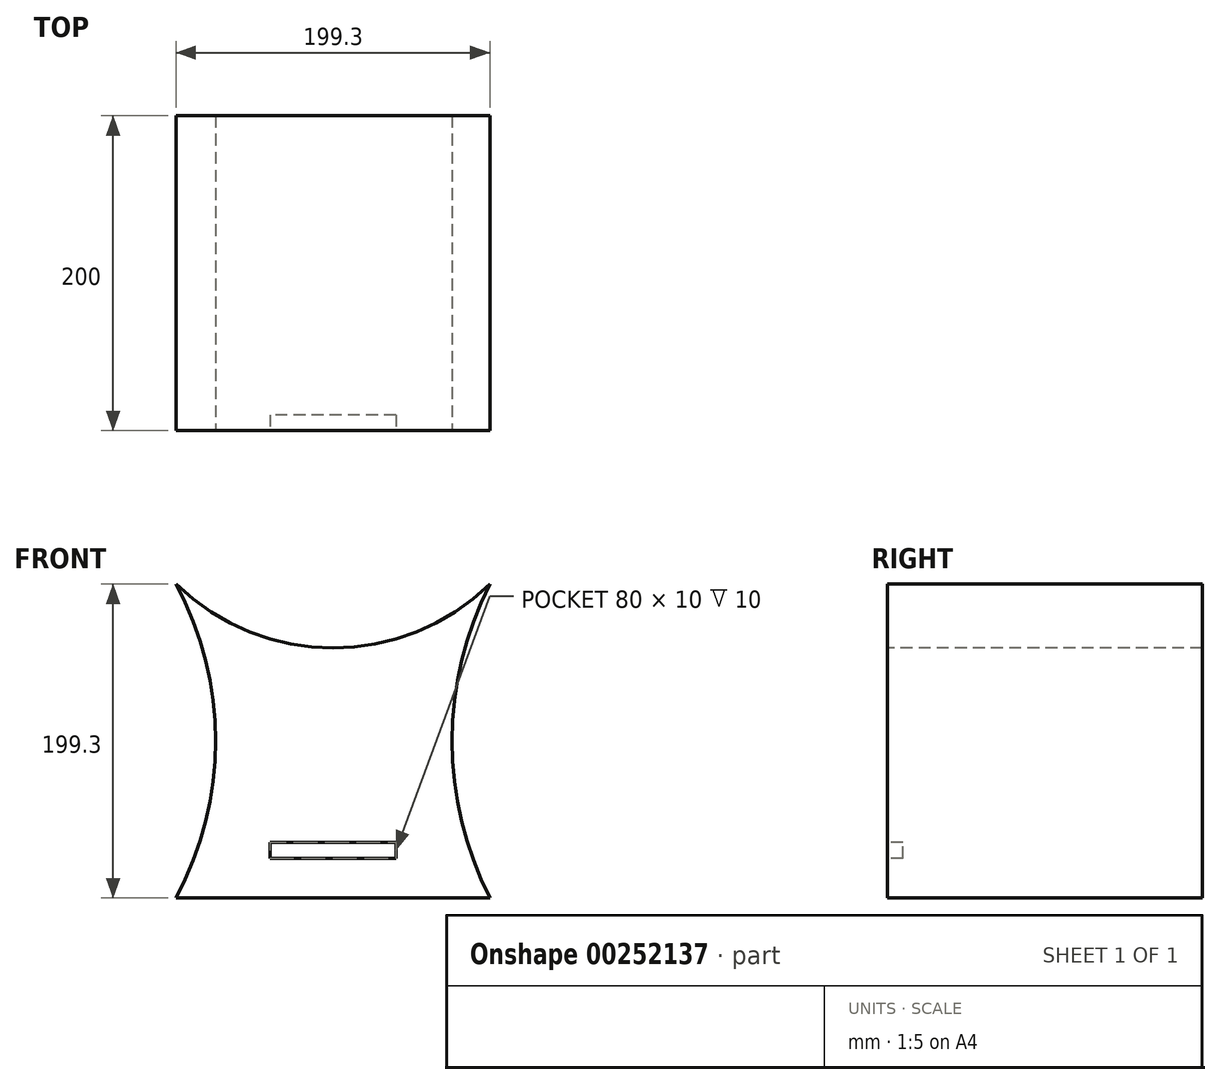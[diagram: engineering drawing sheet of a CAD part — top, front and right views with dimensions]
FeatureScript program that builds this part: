
annotation { "Feature Type Name" : "Feature", "Feature Type Description" : "" }
export const myFeature = defineFeature(function(context is Context, id is Id, definition is map)
    precondition{}
    {
        {
            var Q0;
            Q0=qCreatedBy(makeId("Front.planeOp"),FACE);
            var sketch = newSketch(context, id + "F0", { "sketchPlane" : qUnion([Q0])});
            skLineSegment(sketch, "E0.bottom", {"start": v(99.65, -99.65) * mm, "end": v(-99.65, -99.65) * mm});
            skPoint(sketch, "E0.middle", {"position": v(0, 0) * mm});
            skArc(sketch, "E1", {"start": v(-99.65, 99.65) * mm, "mid": v(0, 59.01) * mm, "end": v(99.65, 99.65) * mm});
            skPoint(sketch, "E1.third.point", {"position": v(107.87, 108.4) * mm});
            skArc(sketch, "E2", {"start": v(-99.65, -99.65) * mm, "mid": v(-74.6, 0) * mm, "end": v(-99.65, 99.65) * mm});
            skPoint(sketch, "E2.third.point", {"position": v(-492.6, 37.65) * mm});
            skArc(sketch, "E3", {"start": v(99.65, 99.65) * mm, "mid": v(75.66, 0) * mm, "end": v(99.65, -99.65) * mm});
            skPoint(sketch, "E3.third.point", {"position": v(336.22, -214.9) * mm});
            skSolve(sketch);
        }
        {
            var Q0;
            Q0=makeQuery(id+"F0.imprint","IMPRINT",FACE,{"disambiguationData":[TD([[makeQuery(id+"F0.imprint","IMPRINT",EDGE,{"derivedFrom":sQuery(id+"F0.wireOp",EDGE,"E0.bottom")}),-1.0]])]});
            extrude(context, id + "F1", {"entities" : qUnion([Q0]), "oppositeDirection" : true, "depth" : 200 * mm});
        }
        {
            var Q0;
            Q0=qCreatedBy(makeId("Front.planeOp"),FACE);
            var sketch = newSketch(context, id + "F2", { "sketchPlane" : qUnion([Q0])});
            skPoint(sketch, "E4", {"position": v(-99.87, -99.58) * mm});
            skPoint(sketch, "E5", {"position": v(100.16, -99.58) * mm});
            skPoint(sketch, "E6", {"position": v(0, -99.58) * mm});
            skLineSegment(sketch, "E7", {"start": v(0, -99.58) * mm, "end": v(0, -69.58) * mm});
            skLineSegment(sketch, "E8.bottom", {"start": v(40, -74.58) * mm, "end": v(-40, -74.58) * mm});
            skLineSegment(sketch, "E8.top", {"start": v(40, -64.58) * mm, "end": v(-40, -64.58) * mm});
            skLineSegment(sketch, "E8.left", {"start": v(40, -74.58) * mm, "end": v(40, -64.58) * mm});
            skLineSegment(sketch, "E8.right", {"start": v(-40, -74.58) * mm, "end": v(-40, -64.58) * mm});
            skPoint(sketch, "E8.middle", {"position": v(0, -69.58) * mm});
            skSolve(sketch);
        }
        {
            var Q0;
            Q0=makeQuery(id+"F2.imprint","IMPRINT",FACE,{"disambiguationData":[TD([[makeQuery(id+"F2.imprint","IMPRINT",EDGE,{"derivedFrom":sQuery(id+"F2.wireOp",EDGE,"E8.top")}),1.0]])]});
            extrude(context, id + "F3", {"entities" : qUnion([Q0]), "operationType" : NewBodyOperationType.REMOVE, "oppositeDirection" : true, "depth" : 10 * mm});
        }
    });
